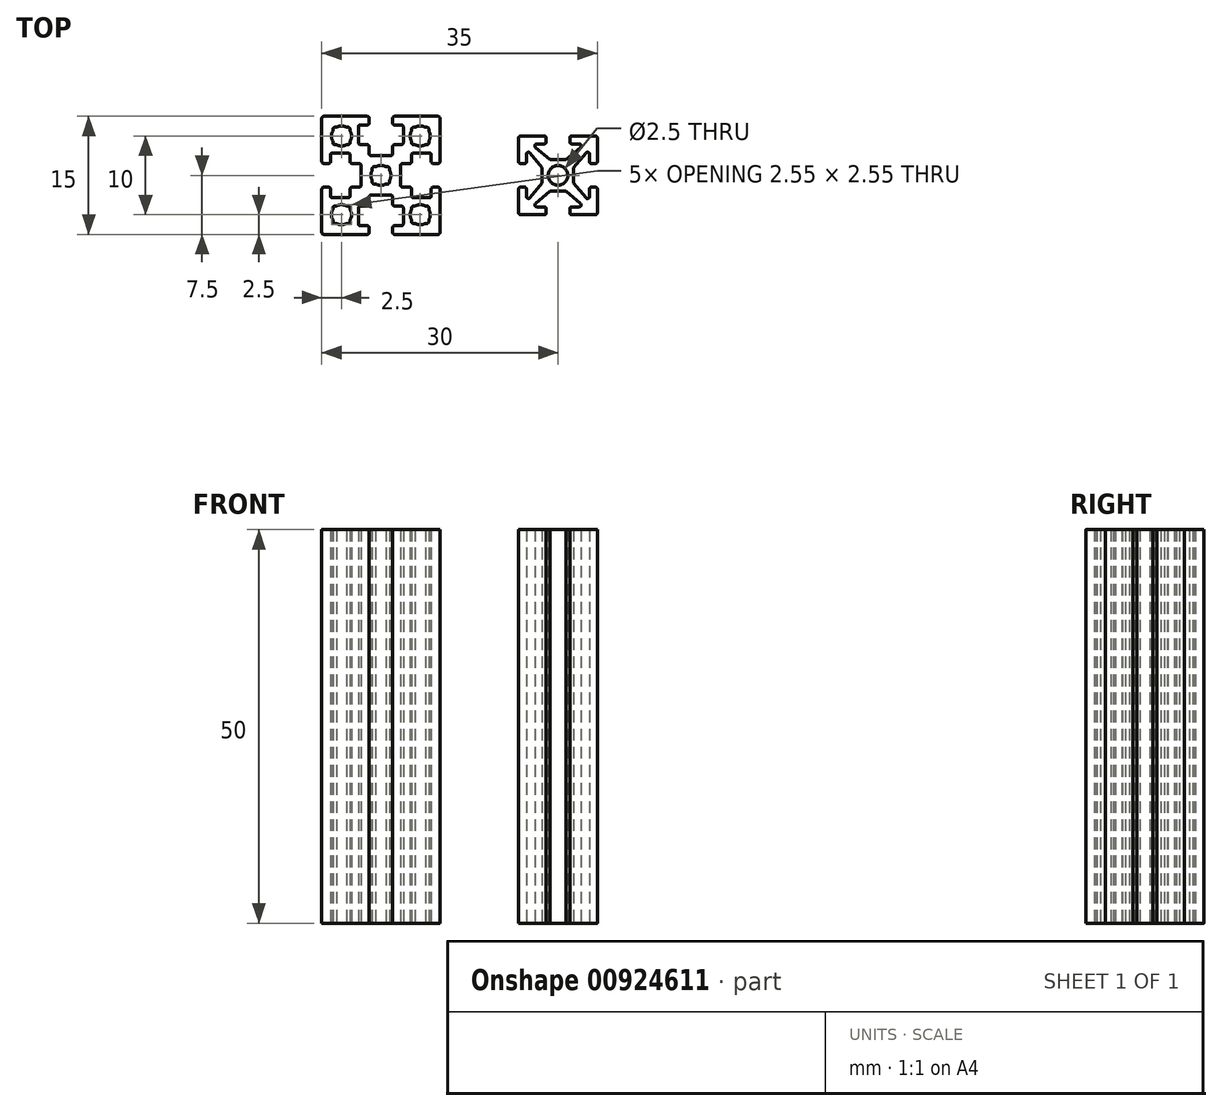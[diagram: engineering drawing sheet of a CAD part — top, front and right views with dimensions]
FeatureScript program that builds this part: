
annotation { "Feature Type Name" : "Feature", "Feature Type Description" : "" }
export const myFeature = defineFeature(function(context is Context, id is Id, definition is map)
    precondition{}
    {
        {
            var Q0;
            Q0=qCreatedBy(makeId("Top.planeOp"),FACE);
            var sketch = newSketch(context, id + "F0", { "sketchPlane" : qUnion([Q0])});
            skLineSegment(sketch, "E0", {"start": v(-7.5, -7.25) * mm, "end": v(-7.5, -1.75) * mm});
            skLineSegment(sketch, "E1", {"start": v(-7.25, -1.5) * mm, "end": v(-6.65, -1.5) * mm});
            skLineSegment(sketch, "E2", {"start": v(-6.4, -1.75) * mm, "end": v(-6.4, -2.6) * mm});
            skLineSegment(sketch, "E3", {"start": v(-6.15, -2.85) * mm, "end": v(-4.15, -2.85) * mm});
            skLineSegment(sketch, "E4", {"start": v(-3.9, -2.6) * mm, "end": v(-3.9, -1.75) * mm});
            skLineSegment(sketch, "E5", {"start": v(-3.65, -1.5) * mm, "end": v(-2.75, -1.5) * mm});
            skLineSegment(sketch, "E6", {"start": v(-2.5, -1.25) * mm, "end": v(-2.5, 0) * mm});
            skLineSegment(sketch, "E7", {"start": v(-7.25, -7.5) * mm, "end": v(-1.75, -7.5) * mm});
            skLineSegment(sketch, "E8", {"start": v(-1.5, -7.25) * mm, "end": v(-1.5, -6.65) * mm});
            skLineSegment(sketch, "E9", {"start": v(-1.75, -6.4) * mm, "end": v(-2.6, -6.4) * mm});
            skLineSegment(sketch, "E10", {"start": v(-2.85, -6.15) * mm, "end": v(-2.85, -4.15) * mm});
            skLineSegment(sketch, "E11", {"start": v(-2.6, -3.9) * mm, "end": v(-1.75, -3.9) * mm});
            skLineSegment(sketch, "E12", {"start": v(-1.5, -3.65) * mm, "end": v(-1.5, -2.75) * mm});
            skLineSegment(sketch, "E13", {"start": v(-1.25, -2.5) * mm, "end": v(0, -2.5) * mm});
            skArc(sketch, "E14", {"start": v(-6.1, -4.36) * mm, "mid": v(-6.27, -5) * mm, "end": v(-6.1, -5.64) * mm});
            skLineSegment(sketch, "E15.bottom", {"start": v(-4.15, -6.1) * mm, "end": v(-4.36, -6.1) * mm});
            skLineSegment(sketch, "E15.top", {"start": v(-4.15, -3.9) * mm, "end": v(-4.36, -3.9) * mm});
            skLineSegment(sketch, "E15.left", {"start": v(-3.9, -5.85) * mm, "end": v(-3.9, -5.64) * mm});
            skLineSegment(sketch, "E15.right", {"start": v(-6.1, -5.85) * mm, "end": v(-6.1, -5.64) * mm});
            skLineSegment(sketch, "E16.trimOffspring", {"start": v(-6.1, -4.36) * mm, "end": v(-6.1, -4.15) * mm});
            skLineSegment(sketch, "E17.trimOffspring", {"start": v(-5.64, -3.9) * mm, "end": v(-5.85, -3.9) * mm});
            skArc(sketch, "E18.trimOffspring", {"start": v(-4.36, -3.9) * mm, "mid": v(-5, -3.73) * mm, "end": v(-5.64, -3.9) * mm});
            skLineSegment(sketch, "E19.trimOffspring", {"start": v(-3.9, -4.36) * mm, "end": v(-3.9, -4.15) * mm});
            skArc(sketch, "E20.trimOffspring", {"start": v(-3.9, -5.64) * mm, "mid": v(-3.72, -5) * mm, "end": v(-3.9, -4.36) * mm});
            skArc(sketch, "E21.trimOffspring", {"start": v(-5.64, -6.1) * mm, "mid": v(-5, -6.28) * mm, "end": v(-4.36, -6.1) * mm});
            skLineSegment(sketch, "E22.trimOffspring", {"start": v(-5.64, -6.1) * mm, "end": v(-5.85, -6.1) * mm});
            skPoint(sketch, "E23.visualSharp", {"position": v(-7.5, -7.5) * mm});
            skArc(sketch, "E23.filletArc", {"start": v(-7.5, -7.25) * mm, "mid": v(-7.43, -7.43) * mm, "end": v(-7.25, -7.5) * mm});
            skPoint(sketch, "E24.visualSharp", {"position": v(-6.1, -6.1) * mm});
            skArc(sketch, "E24.filletArc", {"start": v(-6.1, -5.85) * mm, "mid": v(-6.03, -6.03) * mm, "end": v(-5.85, -6.1) * mm});
            skPoint(sketch, "E25.visualSharp", {"position": v(-6.1, -3.9) * mm});
            skArc(sketch, "E25.filletArc", {"start": v(-5.85, -3.9) * mm, "mid": v(-6.03, -3.97) * mm, "end": v(-6.1, -4.15) * mm});
            skPoint(sketch, "E26.visualSharp", {"position": v(-3.9, -3.9) * mm});
            skArc(sketch, "E26.filletArc", {"start": v(-3.9, -4.15) * mm, "mid": v(-3.97, -3.97) * mm, "end": v(-4.15, -3.9) * mm});
            skPoint(sketch, "E27.visualSharp", {"position": v(-3.9, -6.1) * mm});
            skArc(sketch, "E27.filletArc", {"start": v(-4.15, -6.1) * mm, "mid": v(-3.97, -6.03) * mm, "end": v(-3.9, -5.85) * mm});
            skPoint(sketch, "E28.visualSharp", {"position": v(-7.5, -1.5) * mm});
            skArc(sketch, "E28.filletArc", {"start": v(-7.25, -1.5) * mm, "mid": v(-7.43, -1.57) * mm, "end": v(-7.5, -1.75) * mm});
            skPoint(sketch, "E29.visualSharp", {"position": v(-6.4, -1.5) * mm});
            skArc(sketch, "E29.filletArc", {"start": v(-6.4, -1.75) * mm, "mid": v(-6.47, -1.57) * mm, "end": v(-6.65, -1.5) * mm});
            skPoint(sketch, "E30.visualSharp", {"position": v(-6.4, -2.85) * mm});
            skArc(sketch, "E30.filletArc", {"start": v(-6.4, -2.6) * mm, "mid": v(-6.33, -2.78) * mm, "end": v(-6.15, -2.85) * mm});
            skPoint(sketch, "E31.visualSharp", {"position": v(-3.9, -2.85) * mm});
            skArc(sketch, "E31.filletArc", {"start": v(-4.15, -2.85) * mm, "mid": v(-3.97, -2.78) * mm, "end": v(-3.9, -2.6) * mm});
            skPoint(sketch, "E32.visualSharp", {"position": v(-3.9, -1.5) * mm});
            skArc(sketch, "E32.filletArc", {"start": v(-3.65, -1.5) * mm, "mid": v(-3.83, -1.57) * mm, "end": v(-3.9, -1.75) * mm});
            skPoint(sketch, "E33.visualSharp", {"position": v(-2.5, -1.5) * mm});
            skArc(sketch, "E33.filletArc", {"start": v(-2.75, -1.5) * mm, "mid": v(-2.57, -1.43) * mm, "end": v(-2.5, -1.25) * mm});
            skPoint(sketch, "E34.visualSharp", {"position": v(-1.5, -3.9) * mm});
            skArc(sketch, "E34.filletArc", {"start": v(-1.75, -3.9) * mm, "mid": v(-1.57, -3.83) * mm, "end": v(-1.5, -3.65) * mm});
            skPoint(sketch, "E35.visualSharp", {"position": v(-1.5, -2.5) * mm});
            skArc(sketch, "E35.filletArc", {"start": v(-1.25, -2.5) * mm, "mid": v(-1.43, -2.57) * mm, "end": v(-1.5, -2.75) * mm});
            skPoint(sketch, "E36.visualSharp", {"position": v(-2.85, -3.9) * mm});
            skArc(sketch, "E36.filletArc", {"start": v(-2.6, -3.9) * mm, "mid": v(-2.78, -3.97) * mm, "end": v(-2.85, -4.15) * mm});
            skPoint(sketch, "E37.visualSharp", {"position": v(-2.85, -6.4) * mm});
            skArc(sketch, "E37.filletArc", {"start": v(-2.85, -6.15) * mm, "mid": v(-2.78, -6.33) * mm, "end": v(-2.6, -6.4) * mm});
            skPoint(sketch, "E38.visualSharp", {"position": v(-1.5, -6.4) * mm});
            skArc(sketch, "E38.filletArc", {"start": v(-1.5, -6.65) * mm, "mid": v(-1.57, -6.47) * mm, "end": v(-1.75, -6.4) * mm});
            skPoint(sketch, "E39.visualSharp", {"position": v(-1.5, -7.5) * mm});
            skArc(sketch, "E39.filletArc", {"start": v(-1.75, -7.5) * mm, "mid": v(-1.57, -7.43) * mm, "end": v(-1.5, -7.25) * mm});
            skLineSegment(sketch, "E40", {"start": v(0, 0) * mm, "end": v(0, -7.5) * mm, "construction": true});
            skLineSegment(sketch, "E41.MirrorCS", {"start": v(1.25, -2.5) * mm, "end": v(0, -2.5) * mm});
            skArc(sketch, "E42.MirrorCS", {"start": v(1.25, -2.5) * mm, "mid": v(1.43, -2.57) * mm, "end": v(1.5, -2.75) * mm});
            skLineSegment(sketch, "E43.MirrorCS", {"start": v(1.5, -3.65) * mm, "end": v(1.5, -2.75) * mm});
            skArc(sketch, "E44.MirrorCS", {"start": v(1.75, -3.9) * mm, "mid": v(1.57, -3.83) * mm, "end": v(1.5, -3.65) * mm});
            skLineSegment(sketch, "E45.MirrorCS", {"start": v(2.6, -3.9) * mm, "end": v(1.75, -3.9) * mm});
            skArc(sketch, "E46.MirrorCS", {"start": v(2.6, -3.9) * mm, "mid": v(2.78, -3.97) * mm, "end": v(2.85, -4.15) * mm});
            skLineSegment(sketch, "E47.MirrorCS", {"start": v(2.85, -6.15) * mm, "end": v(2.85, -4.15) * mm});
            skArc(sketch, "E48.MirrorCS", {"start": v(2.85, -6.15) * mm, "mid": v(2.78, -6.33) * mm, "end": v(2.6, -6.4) * mm});
            skLineSegment(sketch, "E49.MirrorCS", {"start": v(1.75, -6.4) * mm, "end": v(2.6, -6.4) * mm});
            skArc(sketch, "E50.MirrorCS", {"start": v(1.5, -6.65) * mm, "mid": v(1.57, -6.47) * mm, "end": v(1.75, -6.4) * mm});
            skLineSegment(sketch, "E51.MirrorCS", {"start": v(1.5, -7.25) * mm, "end": v(1.5, -6.65) * mm});
            skArc(sketch, "E52.MirrorCS", {"start": v(1.75, -7.5) * mm, "mid": v(1.57, -7.43) * mm, "end": v(1.5, -7.25) * mm});
            skLineSegment(sketch, "E53.MirrorCS", {"start": v(7.25, -7.5) * mm, "end": v(1.75, -7.5) * mm});
            skArc(sketch, "E54.MirrorCS", {"start": v(7.5, -7.25) * mm, "mid": v(7.43, -7.43) * mm, "end": v(7.25, -7.5) * mm});
            skLineSegment(sketch, "E55.MirrorCS", {"start": v(7.5, -7.25) * mm, "end": v(7.5, -1.75) * mm});
            skArc(sketch, "E56.MirrorCS", {"start": v(7.25, -1.5) * mm, "mid": v(7.43, -1.57) * mm, "end": v(7.5, -1.75) * mm});
            skLineSegment(sketch, "E57.MirrorCS", {"start": v(7.25, -1.5) * mm, "end": v(6.65, -1.5) * mm});
            skArc(sketch, "E58.MirrorCS", {"start": v(6.4, -1.75) * mm, "mid": v(6.47, -1.57) * mm, "end": v(6.65, -1.5) * mm});
            skLineSegment(sketch, "E59.MirrorCS", {"start": v(6.4, -1.75) * mm, "end": v(6.4, -2.6) * mm});
            skArc(sketch, "E60.MirrorCS", {"start": v(6.4, -2.6) * mm, "mid": v(6.33, -2.78) * mm, "end": v(6.15, -2.85) * mm});
            skLineSegment(sketch, "E61.MirrorCS", {"start": v(6.15, -2.85) * mm, "end": v(4.15, -2.85) * mm});
            skArc(sketch, "E62.MirrorCS", {"start": v(4.15, -2.85) * mm, "mid": v(3.97, -2.78) * mm, "end": v(3.9, -2.6) * mm});
            skLineSegment(sketch, "E63.MirrorCS", {"start": v(3.9, -2.6) * mm, "end": v(3.9, -1.75) * mm});
            skArc(sketch, "E64.MirrorCS", {"start": v(3.65, -1.5) * mm, "mid": v(3.83, -1.57) * mm, "end": v(3.9, -1.75) * mm});
            skLineSegment(sketch, "E65.MirrorCS", {"start": v(3.65, -1.5) * mm, "end": v(2.75, -1.5) * mm});
            skArc(sketch, "E66.MirrorCS", {"start": v(2.75, -1.5) * mm, "mid": v(2.57, -1.43) * mm, "end": v(2.5, -1.25) * mm});
            skLineSegment(sketch, "E67.MirrorCS", {"start": v(2.5, -1.25) * mm, "end": v(2.5, 0) * mm});
            skArc(sketch, "E68.MirrorCS", {"start": v(3.9, -5.64) * mm, "mid": v(3.72, -5) * mm, "end": v(3.9, -4.36) * mm});
            skLineSegment(sketch, "E69.MirrorCS", {"start": v(3.9, -4.36) * mm, "end": v(3.9, -4.15) * mm});
            skArc(sketch, "E70.MirrorCS", {"start": v(3.9, -4.15) * mm, "mid": v(3.97, -3.97) * mm, "end": v(4.15, -3.9) * mm});
            skLineSegment(sketch, "E71.MirrorCS", {"start": v(4.15, -3.9) * mm, "end": v(4.36, -3.9) * mm});
            skArc(sketch, "E72.MirrorCS", {"start": v(4.36, -3.9) * mm, "mid": v(5, -3.73) * mm, "end": v(5.64, -3.9) * mm});
            skLineSegment(sketch, "E73.MirrorCS", {"start": v(5.64, -3.9) * mm, "end": v(5.85, -3.9) * mm});
            skArc(sketch, "E74.MirrorCS", {"start": v(5.85, -3.9) * mm, "mid": v(6.03, -3.97) * mm, "end": v(6.1, -4.15) * mm});
            skLineSegment(sketch, "E75.MirrorCS", {"start": v(6.1, -4.36) * mm, "end": v(6.1, -4.15) * mm});
            skArc(sketch, "E76.MirrorCS", {"start": v(6.1, -4.36) * mm, "mid": v(6.27, -5) * mm, "end": v(6.1, -5.64) * mm});
            skLineSegment(sketch, "E77.MirrorCS", {"start": v(6.1, -5.85) * mm, "end": v(6.1, -5.64) * mm});
            skArc(sketch, "E78.MirrorCS", {"start": v(6.1, -5.85) * mm, "mid": v(6.03, -6.03) * mm, "end": v(5.85, -6.1) * mm});
            skLineSegment(sketch, "E79.MirrorCS", {"start": v(5.64, -6.1) * mm, "end": v(5.85, -6.1) * mm});
            skArc(sketch, "E80.MirrorCS", {"start": v(5.64, -6.1) * mm, "mid": v(5, -6.28) * mm, "end": v(4.36, -6.1) * mm});
            skLineSegment(sketch, "E81.MirrorCS", {"start": v(4.15, -6.1) * mm, "end": v(4.36, -6.1) * mm});
            skArc(sketch, "E82.MirrorCS", {"start": v(4.15, -6.1) * mm, "mid": v(3.97, -6.03) * mm, "end": v(3.9, -5.85) * mm});
            skLineSegment(sketch, "E83.MirrorCS", {"start": v(3.9, -5.85) * mm, "end": v(3.9, -5.64) * mm});
            skLineSegment(sketch, "E84", {"start": v(-7.5, 0) * mm, "end": v(7.5, 0) * mm, "construction": true});
            skLineSegment(sketch, "E85.MirrorCS", {"start": v(-5.64, 6.1) * mm, "end": v(-5.85, 6.1) * mm});
            skLineSegment(sketch, "E86.MirrorCS", {"start": v(-4.15, 3.9) * mm, "end": v(-4.36, 3.9) * mm});
            skArc(sketch, "E87.MirrorCS", {"start": v(-6.1, 5.85) * mm, "mid": v(-6.03, 6.03) * mm, "end": v(-5.85, 6.1) * mm});
            skArc(sketch, "E88.MirrorCS", {"start": v(-5.85, 3.9) * mm, "mid": v(-6.03, 3.97) * mm, "end": v(-6.1, 4.15) * mm});
            skLineSegment(sketch, "E89.MirrorCS", {"start": v(-5.64, 3.9) * mm, "end": v(-5.85, 3.9) * mm});
            skLineSegment(sketch, "E90.MirrorCS", {"start": v(-6.1, 5.85) * mm, "end": v(-6.1, 5.64) * mm});
            skArc(sketch, "E91.MirrorCS", {"start": v(-7.5, 7.25) * mm, "mid": v(-7.43, 7.43) * mm, "end": v(-7.25, 7.5) * mm});
            skLineSegment(sketch, "E92.MirrorCS", {"start": v(-3.9, 5.85) * mm, "end": v(-3.9, 5.64) * mm});
            skLineSegment(sketch, "E93.MirrorCS", {"start": v(-7.25, 1.5) * mm, "end": v(-6.65, 1.5) * mm});
            skArc(sketch, "E94.MirrorCS", {"start": v(-6.4, 2.6) * mm, "mid": v(-6.33, 2.78) * mm, "end": v(-6.15, 2.85) * mm});
            skArc(sketch, "E95.MirrorCS", {"start": v(1.75, 3.9) * mm, "mid": v(1.57, 3.83) * mm, "end": v(1.5, 3.65) * mm});
            skArc(sketch, "E96.MirrorCS", {"start": v(-1.75, 7.5) * mm, "mid": v(-1.57, 7.43) * mm, "end": v(-1.5, 7.25) * mm});
            skLineSegment(sketch, "E97.MirrorCS", {"start": v(3.9, 5.85) * mm, "end": v(3.9, 5.64) * mm});
            skArc(sketch, "E98.MirrorCS", {"start": v(6.4, 2.6) * mm, "mid": v(6.33, 2.78) * mm, "end": v(6.15, 2.85) * mm});
            skArc(sketch, "E99.MirrorCS", {"start": v(-4.15, 6.1) * mm, "mid": v(-3.97, 6.03) * mm, "end": v(-3.9, 5.85) * mm});
            skLineSegment(sketch, "E100.MirrorCS", {"start": v(1.5, 7.25) * mm, "end": v(1.5, 6.65) * mm});
            skLineSegment(sketch, "E101.MirrorCS", {"start": v(-6.1, 4.36) * mm, "end": v(-6.1, 4.15) * mm});
            skArc(sketch, "E102.MirrorCS", {"start": v(-1.25, 2.5) * mm, "mid": v(-1.43, 2.57) * mm, "end": v(-1.5, 2.75) * mm});
            skLineSegment(sketch, "E103.MirrorCS", {"start": v(5.64, 6.1) * mm, "end": v(5.85, 6.1) * mm});
            skArc(sketch, "E104.MirrorCS", {"start": v(-3.65, 1.5) * mm, "mid": v(-3.83, 1.57) * mm, "end": v(-3.9, 1.75) * mm});
            skArc(sketch, "E105.MirrorCS", {"start": v(-6.4, 1.75) * mm, "mid": v(-6.47, 1.57) * mm, "end": v(-6.65, 1.5) * mm});
            skArc(sketch, "E106.MirrorCS", {"start": v(-2.85, 6.15) * mm, "mid": v(-2.78, 6.33) * mm, "end": v(-2.6, 6.4) * mm});
            skLineSegment(sketch, "E107.MirrorCS", {"start": v(4.15, 3.9) * mm, "end": v(4.36, 3.9) * mm});
            skLineSegment(sketch, "E108.MirrorCS", {"start": v(7.25, 1.5) * mm, "end": v(6.65, 1.5) * mm});
            skLineSegment(sketch, "E109.MirrorCS", {"start": v(5.64, 3.9) * mm, "end": v(5.85, 3.9) * mm});
            skArc(sketch, "E110.MirrorCS", {"start": v(2.75, 1.5) * mm, "mid": v(2.57, 1.43) * mm, "end": v(2.5, 1.25) * mm});
            skArc(sketch, "E111.MirrorCS", {"start": v(-2.6, 3.9) * mm, "mid": v(-2.78, 3.97) * mm, "end": v(-2.85, 4.15) * mm});
            skArc(sketch, "E112.MirrorCS", {"start": v(3.65, 1.5) * mm, "mid": v(3.83, 1.57) * mm, "end": v(3.9, 1.75) * mm});
            skArc(sketch, "E113.MirrorCS", {"start": v(6.4, 1.75) * mm, "mid": v(6.47, 1.57) * mm, "end": v(6.65, 1.5) * mm});
            skArc(sketch, "E114.MirrorCS", {"start": v(5.85, 3.9) * mm, "mid": v(6.03, 3.97) * mm, "end": v(6.1, 4.15) * mm});
            skLineSegment(sketch, "E115.MirrorCS", {"start": v(3.9, 4.36) * mm, "end": v(3.9, 4.15) * mm});
            skArc(sketch, "E116.MirrorCS", {"start": v(7.25, 1.5) * mm, "mid": v(7.43, 1.57) * mm, "end": v(7.5, 1.75) * mm});
            skArc(sketch, "E117.MirrorCS", {"start": v(-3.9, 4.15) * mm, "mid": v(-3.97, 3.97) * mm, "end": v(-4.15, 3.9) * mm});
            skArc(sketch, "E118.MirrorCS", {"start": v(-1.75, 3.9) * mm, "mid": v(-1.57, 3.83) * mm, "end": v(-1.5, 3.65) * mm});
            skArc(sketch, "E119.MirrorCS", {"start": v(4.15, 2.85) * mm, "mid": v(3.97, 2.78) * mm, "end": v(3.9, 2.6) * mm});
            skArc(sketch, "E120.MirrorCS", {"start": v(1.25, 2.5) * mm, "mid": v(1.43, 2.57) * mm, "end": v(1.5, 2.75) * mm});
            skLineSegment(sketch, "E121.MirrorCS", {"start": v(6.1, 4.36) * mm, "end": v(6.1, 4.15) * mm});
            skLineSegment(sketch, "E122.MirrorCS", {"start": v(-3.9, 4.36) * mm, "end": v(-3.9, 4.15) * mm});
            skArc(sketch, "E123.MirrorCS", {"start": v(-1.5, 6.65) * mm, "mid": v(-1.57, 6.47) * mm, "end": v(-1.75, 6.4) * mm});
            skArc(sketch, "E124.MirrorCS", {"start": v(2.6, 3.9) * mm, "mid": v(2.78, 3.97) * mm, "end": v(2.85, 4.15) * mm});
            skArc(sketch, "E125.MirrorCS", {"start": v(7.5, 7.25) * mm, "mid": v(7.43, 7.43) * mm, "end": v(7.25, 7.5) * mm});
            skArc(sketch, "E126.MirrorCS", {"start": v(3.9, 4.15) * mm, "mid": v(3.97, 3.97) * mm, "end": v(4.15, 3.9) * mm});
            skArc(sketch, "E127.MirrorCS", {"start": v(1.5, 6.65) * mm, "mid": v(1.57, 6.47) * mm, "end": v(1.75, 6.4) * mm});
            skArc(sketch, "E128.MirrorCS", {"start": v(6.1, 5.85) * mm, "mid": v(6.03, 6.03) * mm, "end": v(5.85, 6.1) * mm});
            skLineSegment(sketch, "E129.MirrorCS", {"start": v(4.15, 6.1) * mm, "end": v(4.36, 6.1) * mm});
            skArc(sketch, "E130.MirrorCS", {"start": v(-2.75, 1.5) * mm, "mid": v(-2.57, 1.43) * mm, "end": v(-2.5, 1.25) * mm});
            skArc(sketch, "E131.MirrorCS", {"start": v(-4.15, 2.85) * mm, "mid": v(-3.97, 2.78) * mm, "end": v(-3.9, 2.6) * mm});
            skArc(sketch, "E132.MirrorCS", {"start": v(1.75, 7.5) * mm, "mid": v(1.57, 7.43) * mm, "end": v(1.5, 7.25) * mm});
            skLineSegment(sketch, "E133.MirrorCS", {"start": v(6.1, 5.85) * mm, "end": v(6.1, 5.64) * mm});
            skLineSegment(sketch, "E134.MirrorCS", {"start": v(-1.5, 7.25) * mm, "end": v(-1.5, 6.65) * mm});
            skArc(sketch, "E135.MirrorCS", {"start": v(2.85, 6.15) * mm, "mid": v(2.78, 6.33) * mm, "end": v(2.6, 6.4) * mm});
            skLineSegment(sketch, "E136.MirrorCS", {"start": v(-4.15, 6.1) * mm, "end": v(-4.36, 6.1) * mm});
            skArc(sketch, "E137.MirrorCS", {"start": v(-7.25, 1.5) * mm, "mid": v(-7.43, 1.57) * mm, "end": v(-7.5, 1.75) * mm});
            skArc(sketch, "E138.MirrorCS", {"start": v(4.15, 6.1) * mm, "mid": v(3.97, 6.03) * mm, "end": v(3.9, 5.85) * mm});
            skLineSegment(sketch, "E139.MirrorCS", {"start": v(2.6, 3.9) * mm, "end": v(1.75, 3.9) * mm});
            skPoint(sketch, "E140.MirrorP", {"position": v(-3.9, 6.1) * mm});
            skPoint(sketch, "E141.MirrorP", {"position": v(-1.5, 2.5) * mm});
            skLineSegment(sketch, "E142.MirrorCS", {"start": v(1.5, 3.65) * mm, "end": v(1.5, 2.75) * mm});
            skLineSegment(sketch, "E143.MirrorCS", {"start": v(-1.75, 6.4) * mm, "end": v(-2.6, 6.4) * mm});
            skPoint(sketch, "E144.MirrorP", {"position": v(-2.85, 6.4) * mm});
            skLineSegment(sketch, "E145.MirrorCS", {"start": v(3.65, 1.5) * mm, "end": v(2.75, 1.5) * mm});
            skPoint(sketch, "E146.MirrorP", {"position": v(-7.5, 7.5) * mm});
            skArc(sketch, "E147.MirrorCS", {"start": v(6.1, 4.36) * mm, "mid": v(6.27, 5) * mm, "end": v(6.1, 5.64) * mm});
            skPoint(sketch, "E148.MirrorP", {"position": v(-3.9, 3.9) * mm});
            skArc(sketch, "E149.MirrorCS", {"start": v(3.9, 5.64) * mm, "mid": v(3.72, 5) * mm, "end": v(3.9, 4.36) * mm});
            skPoint(sketch, "E150.MirrorP", {"position": v(-3.9, 2.85) * mm});
            skLineSegment(sketch, "E151.MirrorCS", {"start": v(-6.15, 2.85) * mm, "end": v(-4.15, 2.85) * mm});
            skLineSegment(sketch, "E152.MirrorCS", {"start": v(-2.85, 6.15) * mm, "end": v(-2.85, 4.15) * mm});
            skArc(sketch, "E153.MirrorCS", {"start": v(-3.9, 5.64) * mm, "mid": v(-3.72, 5) * mm, "end": v(-3.9, 4.36) * mm});
            skLineSegment(sketch, "E154.MirrorCS", {"start": v(-3.9, 2.6) * mm, "end": v(-3.9, 1.75) * mm});
            skPoint(sketch, "E155.MirrorP", {"position": v(-6.4, 2.85) * mm});
            skLineSegment(sketch, "E156.MirrorCS", {"start": v(1.25, 2.5) * mm, "end": v(0, 2.5) * mm});
            skArc(sketch, "E157.MirrorCS", {"start": v(-6.1, 4.36) * mm, "mid": v(-6.27, 5) * mm, "end": v(-6.1, 5.64) * mm});
            skArc(sketch, "E158.MirrorCS", {"start": v(5.64, 6.1) * mm, "mid": v(5, 6.28) * mm, "end": v(4.36, 6.1) * mm});
            skPoint(sketch, "E159.MirrorP", {"position": v(-6.1, 6.1) * mm});
            skPoint(sketch, "E160.MirrorP", {"position": v(-2.85, 3.9) * mm});
            skArc(sketch, "E161.MirrorCS", {"start": v(-5.64, 6.1) * mm, "mid": v(-5, 6.28) * mm, "end": v(-4.36, 6.1) * mm});
            skPoint(sketch, "E162.MirrorP", {"position": v(-1.5, 3.9) * mm});
            skLineSegment(sketch, "E163.MirrorCS", {"start": v(-7.5, 7.25) * mm, "end": v(-7.5, 1.75) * mm});
            skLineSegment(sketch, "E164.MirrorCS", {"start": v(6.4, 1.75) * mm, "end": v(6.4, 2.6) * mm});
            skPoint(sketch, "E165.MirrorP", {"position": v(-6.1, 3.9) * mm});
            skLineSegment(sketch, "E166.MirrorCS", {"start": v(-3.65, 1.5) * mm, "end": v(-2.75, 1.5) * mm});
            skLineSegment(sketch, "E167.MirrorCS", {"start": v(6.15, 2.85) * mm, "end": v(4.15, 2.85) * mm});
            skPoint(sketch, "E168.MirrorP", {"position": v(-1.5, 7.5) * mm});
            skPoint(sketch, "E169.MirrorP", {"position": v(-1.5, 6.4) * mm});
            skLineSegment(sketch, "E170.MirrorCS", {"start": v(-7.25, 7.5) * mm, "end": v(-1.75, 7.5) * mm});
            skPoint(sketch, "E171.MirrorP", {"position": v(-7.5, 1.5) * mm});
            skPoint(sketch, "E172.MirrorP", {"position": v(-6.4, 1.5) * mm});
            skLineSegment(sketch, "E173.MirrorCS", {"start": v(-1.5, 3.65) * mm, "end": v(-1.5, 2.75) * mm});
            skArc(sketch, "E174.MirrorCS", {"start": v(4.36, 3.9) * mm, "mid": v(5, 3.73) * mm, "end": v(5.64, 3.9) * mm});
            skPoint(sketch, "E175.MirrorP", {"position": v(-2.5, 1.5) * mm});
            skLineSegment(sketch, "E176.MirrorCS", {"start": v(2.85, 6.15) * mm, "end": v(2.85, 4.15) * mm});
            skLineSegment(sketch, "E177.MirrorCS", {"start": v(1.75, 6.4) * mm, "end": v(2.6, 6.4) * mm});
            skLineSegment(sketch, "E178.MirrorCS", {"start": v(-6.4, 1.75) * mm, "end": v(-6.4, 2.6) * mm});
            skLineSegment(sketch, "E179.MirrorCS", {"start": v(-1.25, 2.5) * mm, "end": v(0, 2.5) * mm});
            skLineSegment(sketch, "E180.MirrorCS", {"start": v(7.5, 7.25) * mm, "end": v(7.5, 1.75) * mm});
            skArc(sketch, "E181.MirrorCS", {"start": v(-4.36, 3.9) * mm, "mid": v(-5, 3.73) * mm, "end": v(-5.64, 3.9) * mm});
            skLineSegment(sketch, "E182.MirrorCS", {"start": v(7.25, 7.5) * mm, "end": v(1.75, 7.5) * mm});
            skPoint(sketch, "E183.MirrorP", {"position": v(-3.9, 1.5) * mm});
            skLineSegment(sketch, "E184.MirrorCS", {"start": v(3.9, 2.6) * mm, "end": v(3.9, 1.75) * mm});
            skLineSegment(sketch, "E185.MirrorCS", {"start": v(-2.6, 3.9) * mm, "end": v(-1.75, 3.9) * mm});
            skLineSegment(sketch, "E186.MirrorCS", {"start": v(-2.5, 1.25) * mm, "end": v(-2.5, 0) * mm});
            skLineSegment(sketch, "E187.MirrorCS", {"start": v(2.5, 1.25) * mm, "end": v(2.5, 0) * mm});
            skArc(sketch, "E188", {"start": v(-1.1, 0.64) * mm, "mid": v(-1.27, 0) * mm, "end": v(-1.1, -0.64) * mm});
            skLineSegment(sketch, "E189.bottom", {"start": v(0.85, -1.1) * mm, "end": v(0.64, -1.1) * mm});
            skLineSegment(sketch, "E189.top", {"start": v(0.85, 1.1) * mm, "end": v(0.64, 1.1) * mm});
            skLineSegment(sketch, "E189.left", {"start": v(1.1, -0.85) * mm, "end": v(1.1, -0.64) * mm});
            skLineSegment(sketch, "E189.right", {"start": v(-1.1, -0.85) * mm, "end": v(-1.1, -0.64) * mm});
            skLineSegment(sketch, "E190.trimOffspring", {"start": v(-1.1, 0.64) * mm, "end": v(-1.1, 0.85) * mm});
            skLineSegment(sketch, "E191.trimOffspring", {"start": v(-0.64, 1.1) * mm, "end": v(-0.85, 1.1) * mm});
            skArc(sketch, "E192.trimOffspring", {"start": v(0.64, 1.1) * mm, "mid": v(0, 1.27) * mm, "end": v(-0.64, 1.1) * mm});
            skLineSegment(sketch, "E193.trimOffspring", {"start": v(1.1, 0.64) * mm, "end": v(1.1, 0.85) * mm});
            skArc(sketch, "E194.trimOffspring", {"start": v(1.1, -0.64) * mm, "mid": v(1.27, 0) * mm, "end": v(1.1, 0.64) * mm});
            skArc(sketch, "E195.trimOffspring", {"start": v(-0.64, -1.1) * mm, "mid": v(0, -1.27) * mm, "end": v(0.64, -1.1) * mm});
            skLineSegment(sketch, "E196.trimOffspring", {"start": v(-0.64, -1.1) * mm, "end": v(-0.85, -1.1) * mm});
            skPoint(sketch, "E197.visualSharp", {"position": v(-1.1, -1.1) * mm});
            skArc(sketch, "E197.filletArc", {"start": v(-1.1, -0.85) * mm, "mid": v(-1.03, -1.03) * mm, "end": v(-0.85, -1.1) * mm});
            skPoint(sketch, "E198.visualSharp", {"position": v(-1.1, 1.1) * mm});
            skArc(sketch, "E198.filletArc", {"start": v(-0.85, 1.1) * mm, "mid": v(-1.03, 1.03) * mm, "end": v(-1.1, 0.85) * mm});
            skPoint(sketch, "E199.visualSharp", {"position": v(1.1, 1.1) * mm});
            skArc(sketch, "E199.filletArc", {"start": v(1.1, 0.85) * mm, "mid": v(1.03, 1.03) * mm, "end": v(0.85, 1.1) * mm});
            skPoint(sketch, "E200.visualSharp", {"position": v(1.1, -1.1) * mm});
            skArc(sketch, "E200.filletArc", {"start": v(0.85, -1.1) * mm, "mid": v(1.03, -1.03) * mm, "end": v(1.1, -0.85) * mm});
            skLineSegment(sketch, "E201", {"start": v(17.5, -1.75) * mm, "end": v(17.5, -4.75) * mm});
            skLineSegment(sketch, "E202", {"start": v(17.75, -5) * mm, "end": v(20.75, -5) * mm});
            skLineSegment(sketch, "E203", {"start": v(21, -4.75) * mm, "end": v(21, -4.25) * mm});
            skLineSegment(sketch, "E204", {"start": v(20.75, -4) * mm, "end": v(19.8, -4) * mm});
            skLineSegment(sketch, "E205", {"start": v(19.65, -3.56) * mm, "end": v(21.5, -2) * mm});
            skLineSegment(sketch, "E206", {"start": v(21.5, -2) * mm, "end": v(22.5, -2) * mm});
            skLineSegment(sketch, "E207", {"start": v(17.75, -1.5) * mm, "end": v(18.25, -1.5) * mm});
            skLineSegment(sketch, "E208", {"start": v(18.5, -1.75) * mm, "end": v(18.5, -2.7) * mm});
            skLineSegment(sketch, "E209", {"start": v(18.94, -2.85) * mm, "end": v(20.5, -1) * mm});
            skLineSegment(sketch, "E210", {"start": v(20.5, -1) * mm, "end": v(20.5, 0) * mm});
            skPoint(sketch, "E211.visualSharp", {"position": v(21, -5) * mm});
            skArc(sketch, "E211.filletArc", {"start": v(20.75, -5) * mm, "mid": v(20.93, -4.93) * mm, "end": v(21, -4.75) * mm});
            skPoint(sketch, "E212.visualSharp", {"position": v(21, -4) * mm});
            skArc(sketch, "E212.filletArc", {"start": v(21, -4.25) * mm, "mid": v(20.93, -4.07) * mm, "end": v(20.75, -4) * mm});
            skPoint(sketch, "E213.visualSharp", {"position": v(19.12, -4) * mm});
            skArc(sketch, "E213.filletArc", {"start": v(19.65, -3.56) * mm, "mid": v(19.57, -3.84) * mm, "end": v(19.8, -4) * mm});
            skPoint(sketch, "E214.visualSharp", {"position": v(17.5, -5) * mm});
            skArc(sketch, "E214.filletArc", {"start": v(17.5, -4.75) * mm, "mid": v(17.57, -4.93) * mm, "end": v(17.75, -5) * mm});
            skPoint(sketch, "E215.visualSharp", {"position": v(17.5, -1.5) * mm});
            skArc(sketch, "E215.filletArc", {"start": v(17.75, -1.5) * mm, "mid": v(17.57, -1.57) * mm, "end": v(17.5, -1.75) * mm});
            skPoint(sketch, "E216.visualSharp", {"position": v(18.5, -1.5) * mm});
            skArc(sketch, "E216.filletArc", {"start": v(18.5, -1.75) * mm, "mid": v(18.43, -1.57) * mm, "end": v(18.25, -1.5) * mm});
            skPoint(sketch, "E217.visualSharp", {"position": v(18.5, -3.38) * mm});
            skArc(sketch, "E217.filletArc", {"start": v(18.5, -2.7) * mm, "mid": v(18.66, -2.93) * mm, "end": v(18.94, -2.85) * mm});
            skCircle(sketch, "E218", {"center": v(22.5, 0) * mm, "radius": 1.25 * mm});
            skLineSegment(sketch, "E219", {"start": v(22.5, 0) * mm, "end": v(22.5, -5) * mm, "construction": true});
            skLineSegment(sketch, "E220", {"start": v(22.5, 0) * mm, "end": v(17.5, 0) * mm, "construction": true});
            skLineSegment(sketch, "E221.MirrorCS", {"start": v(23.5, -2) * mm, "end": v(22.5, -2) * mm});
            skLineSegment(sketch, "E222.MirrorCS", {"start": v(25.35, -3.56) * mm, "end": v(23.5, -2) * mm});
            skLineSegment(sketch, "E223.MirrorCS", {"start": v(24.25, -4) * mm, "end": v(25.2, -4) * mm});
            skArc(sketch, "E224.MirrorCS", {"start": v(25.35, -3.56) * mm, "mid": v(25.43, -3.84) * mm, "end": v(25.2, -4) * mm});
            skArc(sketch, "E225.MirrorCS", {"start": v(24, -4.25) * mm, "mid": v(24.07, -4.07) * mm, "end": v(24.25, -4) * mm});
            skLineSegment(sketch, "E226.MirrorCS", {"start": v(24, -4.75) * mm, "end": v(24, -4.25) * mm});
            skArc(sketch, "E227.MirrorCS", {"start": v(24.25, -5) * mm, "mid": v(24.07, -4.93) * mm, "end": v(24, -4.75) * mm});
            skLineSegment(sketch, "E228.MirrorCS", {"start": v(27.25, -5) * mm, "end": v(24.25, -5) * mm});
            skArc(sketch, "E229.MirrorCS", {"start": v(27.5, -4.75) * mm, "mid": v(27.43, -4.93) * mm, "end": v(27.25, -5) * mm});
            skLineSegment(sketch, "E230.MirrorCS", {"start": v(27.5, -1.75) * mm, "end": v(27.5, -4.75) * mm});
            skArc(sketch, "E231.MirrorCS", {"start": v(27.25, -1.5) * mm, "mid": v(27.43, -1.57) * mm, "end": v(27.5, -1.75) * mm});
            skLineSegment(sketch, "E232.MirrorCS", {"start": v(27.25, -1.5) * mm, "end": v(26.75, -1.5) * mm});
            skArc(sketch, "E233.MirrorCS", {"start": v(26.5, -1.75) * mm, "mid": v(26.57, -1.57) * mm, "end": v(26.75, -1.5) * mm});
            skLineSegment(sketch, "E234.MirrorCS", {"start": v(26.5, -1.75) * mm, "end": v(26.5, -2.7) * mm});
            skArc(sketch, "E235.MirrorCS", {"start": v(26.5, -2.7) * mm, "mid": v(26.34, -2.93) * mm, "end": v(26.06, -2.85) * mm});
            skLineSegment(sketch, "E236.MirrorCS", {"start": v(26.06, -2.85) * mm, "end": v(24.5, -1) * mm});
            skLineSegment(sketch, "E237.MirrorCS", {"start": v(24.5, -1) * mm, "end": v(24.5, 0) * mm});
            skArc(sketch, "E238.MirrorCS", {"start": v(18.5, 1.75) * mm, "mid": v(18.43, 1.57) * mm, "end": v(18.25, 1.5) * mm});
            skArc(sketch, "E239.MirrorCS", {"start": v(20.75, 5) * mm, "mid": v(20.93, 4.93) * mm, "end": v(21, 4.75) * mm});
            skArc(sketch, "E240.MirrorCS", {"start": v(27.25, 1.5) * mm, "mid": v(27.43, 1.57) * mm, "end": v(27.5, 1.75) * mm});
            skArc(sketch, "E241.MirrorCS", {"start": v(26.5, 1.75) * mm, "mid": v(26.57, 1.57) * mm, "end": v(26.75, 1.5) * mm});
            skArc(sketch, "E242.MirrorCS", {"start": v(21, 4.25) * mm, "mid": v(20.93, 4.07) * mm, "end": v(20.75, 4) * mm});
            skArc(sketch, "E243.MirrorCS", {"start": v(24, 4.25) * mm, "mid": v(24.07, 4.07) * mm, "end": v(24.25, 4) * mm});
            skArc(sketch, "E244.MirrorCS", {"start": v(24.25, 5) * mm, "mid": v(24.07, 4.93) * mm, "end": v(24, 4.75) * mm});
            skArc(sketch, "E245.MirrorCS", {"start": v(17.5, 4.75) * mm, "mid": v(17.57, 4.93) * mm, "end": v(17.75, 5) * mm});
            skArc(sketch, "E246.MirrorCS", {"start": v(17.75, 1.5) * mm, "mid": v(17.57, 1.57) * mm, "end": v(17.5, 1.75) * mm});
            skArc(sketch, "E247.MirrorCS", {"start": v(27.5, 4.75) * mm, "mid": v(27.43, 4.93) * mm, "end": v(27.25, 5) * mm});
            skLineSegment(sketch, "E248.MirrorCS", {"start": v(18.5, 1.75) * mm, "end": v(18.5, 2.7) * mm});
            skPoint(sketch, "E249.MirrorP", {"position": v(17.5, 5) * mm});
            skPoint(sketch, "E250.MirrorP", {"position": v(17.5, 1.5) * mm});
            skLineSegment(sketch, "E251.MirrorCS", {"start": v(23.5, 2) * mm, "end": v(22.5, 2) * mm});
            skLineSegment(sketch, "E252.MirrorCS", {"start": v(25.35, 3.56) * mm, "end": v(23.5, 2) * mm});
            skArc(sketch, "E253.MirrorCS", {"start": v(18.5, 2.7) * mm, "mid": v(18.66, 2.93) * mm, "end": v(18.94, 2.85) * mm});
            skLineSegment(sketch, "E254.MirrorCS", {"start": v(26.5, 1.75) * mm, "end": v(26.5, 2.7) * mm});
            skArc(sketch, "E255.MirrorCS", {"start": v(25.35, 3.56) * mm, "mid": v(25.43, 3.84) * mm, "end": v(25.2, 4) * mm});
            skLineSegment(sketch, "E256.MirrorCS", {"start": v(17.75, 5) * mm, "end": v(20.75, 5) * mm});
            skLineSegment(sketch, "E257.MirrorCS", {"start": v(21.5, 2) * mm, "end": v(22.5, 2) * mm});
            skLineSegment(sketch, "E258.MirrorCS", {"start": v(27.25, 5) * mm, "end": v(24.25, 5) * mm});
            skLineSegment(sketch, "E259.MirrorCS", {"start": v(27.25, 1.5) * mm, "end": v(26.75, 1.5) * mm});
            skLineSegment(sketch, "E260.MirrorCS", {"start": v(21, 4.75) * mm, "end": v(21, 4.25) * mm});
            skPoint(sketch, "E261.MirrorP", {"position": v(21, 4) * mm});
            skArc(sketch, "E262.MirrorCS", {"start": v(26.5, 2.7) * mm, "mid": v(26.34, 2.93) * mm, "end": v(26.06, 2.85) * mm});
            skPoint(sketch, "E263.MirrorP", {"position": v(18.5, 1.5) * mm});
            skPoint(sketch, "E264.MirrorP", {"position": v(18.5, 3.38) * mm});
            skLineSegment(sketch, "E265.MirrorCS", {"start": v(24, 4.75) * mm, "end": v(24, 4.25) * mm});
            skLineSegment(sketch, "E266.MirrorCS", {"start": v(27.5, 1.75) * mm, "end": v(27.5, 4.75) * mm});
            skLineSegment(sketch, "E267.MirrorCS", {"start": v(19.65, 3.56) * mm, "end": v(21.5, 2) * mm});
            skLineSegment(sketch, "E268.MirrorCS", {"start": v(17.75, 1.5) * mm, "end": v(18.25, 1.5) * mm});
            skLineSegment(sketch, "E269.MirrorCS", {"start": v(24.25, 4) * mm, "end": v(25.2, 4) * mm});
            skPoint(sketch, "E270.MirrorP", {"position": v(21, 5) * mm});
            skLineSegment(sketch, "E271.MirrorCS", {"start": v(26.06, 2.85) * mm, "end": v(24.5, 1) * mm});
            skLineSegment(sketch, "E272.MirrorCS", {"start": v(18.94, 2.85) * mm, "end": v(20.5, 1) * mm});
            skPoint(sketch, "E273.MirrorP", {"position": v(19.12, 4) * mm});
            skArc(sketch, "E274.MirrorCS", {"start": v(19.65, 3.56) * mm, "mid": v(19.57, 3.84) * mm, "end": v(19.8, 4) * mm});
            skLineSegment(sketch, "E275.MirrorCS", {"start": v(17.5, 1.75) * mm, "end": v(17.5, 4.75) * mm});
            skLineSegment(sketch, "E276.MirrorCS", {"start": v(20.75, 4) * mm, "end": v(19.8, 4) * mm});
            skLineSegment(sketch, "E277.MirrorCS", {"start": v(20.5, 1) * mm, "end": v(20.5, 0) * mm});
            skLineSegment(sketch, "E278.MirrorCS", {"start": v(24.5, 1) * mm, "end": v(24.5, 0) * mm});
            skSolve(sketch);
        }
        {
            var Q0;
            Q0=makeQuery(id+"F0.imprint","IMPRINT",FACE,{"disambiguationData":[TD([[makeQuery(id+"F0.imprint","IMPRINT",EDGE,{"derivedFrom":sQuery(id+"F0.wireOp",EDGE,"E0")}),-1.0]])]});
            var Q1;
            Q1=makeQuery(id+"F0.imprint","IMPRINT",FACE,{"disambiguationData":[TD([[makeQuery(id+"F0.imprint","IMPRINT",EDGE,{"derivedFrom":sQuery(id+"F0.wireOp",EDGE,"E201")}),1.0]])]});
            extrude(context, id + "F1", {"entities" : qUnion([Q0, Q1]), "depth" : 50 * mm, "offsetDistance" : 25 * mm});
        }
    });
